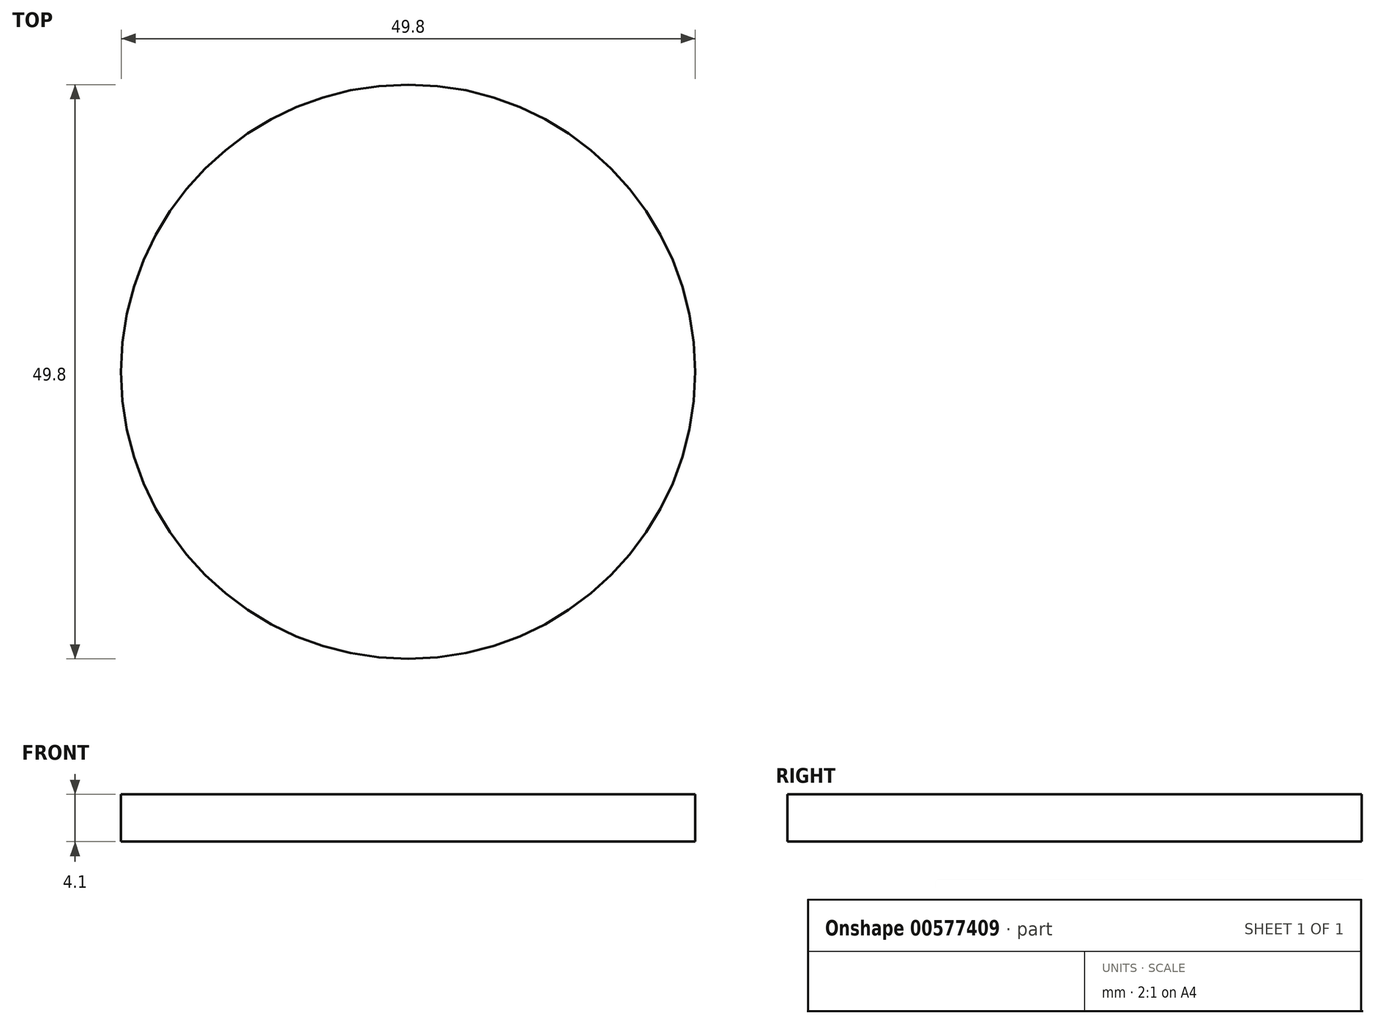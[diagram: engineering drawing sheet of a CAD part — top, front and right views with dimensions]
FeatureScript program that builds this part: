
annotation { "Feature Type Name" : "Feature", "Feature Type Description" : "" }
export const myFeature = defineFeature(function(context is Context, id is Id, definition is map)
    precondition{}
    {
        {
            var Q0;
            Q0=qCreatedBy(makeId("Top.planeOp"),FACE);
            var sketch = newSketch(context, id + "F0", { "sketchPlane" : qUnion([Q0])});
            skCircle(sketch, "E0", {"center": v(0, 0) * mm, "radius": 24.9 * mm});
            skSolve(sketch);
        }
        {
            var Q0;
            Q0=makeQuery(id+"F0.imprint","IMPRINT",FACE,{"disambiguationData":[TD([[makeQuery(id+"F0.imprint","IMPRINT",EDGE,{"derivedFrom":sQuery(id+"F0.wireOp",EDGE,"E0")}),1.0]])]});
            extrude(context, id + "F1", {"entities" : qUnion([Q0]), "depth" : 4.1 * mm, "offsetDistance" : 25 * mm});
        }
    });
